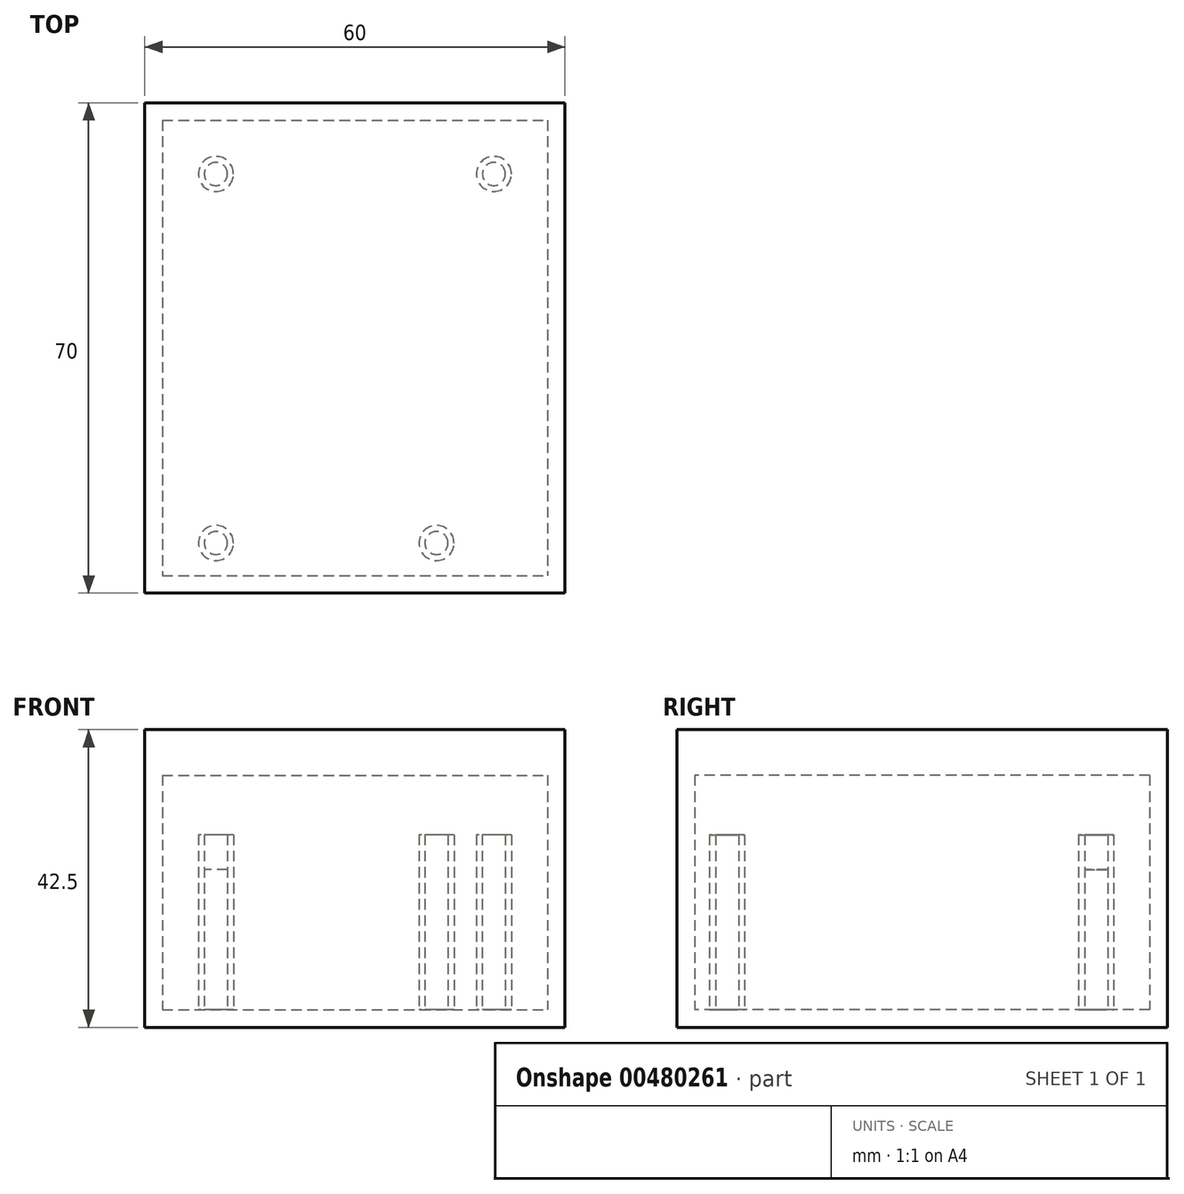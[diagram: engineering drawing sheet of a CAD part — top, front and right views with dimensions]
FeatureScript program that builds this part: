
annotation { "Feature Type Name" : "Feature", "Feature Type Description" : "" }
export const myFeature = defineFeature(function(context is Context, id is Id, definition is map)
    precondition{}
    {
        {
            var Q0;
            Q0=qCreatedBy(makeId("Top.planeOp"),FACE);
            var sketch = newSketch(context, id + "F0", { "sketchPlane" : qUnion([Q0])});
            skLineSegment(sketch, "E0.bottom", {"start": v(-30, 35) * mm, "end": v(30, 35) * mm});
            skLineSegment(sketch, "E0.top", {"start": v(-30, -35) * mm, "end": v(30, -35) * mm});
            skLineSegment(sketch, "E0.left", {"start": v(-30, 35) * mm, "end": v(-30, -35) * mm});
            skLineSegment(sketch, "E0.right", {"start": v(30, 35) * mm, "end": v(30, -35) * mm});
            skPoint(sketch, "E0.middle", {"position": v(0, 0) * mm});
            skSolve(sketch);
        }
        {
            var Q0;
            Q0=makeQuery(id+"F0.imprint","IMPRINT",FACE,{"disambiguationData":[TD([[makeQuery(id+"F0.imprint","IMPRINT",EDGE,{"derivedFrom":sQuery(id+"F0.wireOp",EDGE,"E0.bottom")}),-1.0]])]});
            extrude(context, id + "F1", {"entities" : qUnion([Q0]), "depth" : 40 * mm});
        }
        {
            var Q0;
            Q0=makeQuery(id+"F1.opExtrude","CAP_FACE",FACE,{"disambiguationData":[OSD([sQuery(id+"F0.wireOp",EDGE,"E0.bottom"),sQuery(id+"F0.wireOp",EDGE,"E0.top"),sQuery(id+"F0.wireOp",EDGE,"E0.left"),sQuery(id+"F0.wireOp",EDGE,"E0.right")])],"isStart":false});
            shell(context, id + "F2", {"entities" : qUnion([Q0]), "thickness" : 2.5 * mm});
        }
        {
            var Q0;
            Q0=makeQuery(id+"F1.opExtrude","CAP_FACE",FACE,{"disambiguationData":[OSD([sQuery(id+"F0.wireOp",EDGE,"E0.bottom"),sQuery(id+"F0.wireOp",EDGE,"E0.top"),sQuery(id+"F0.wireOp",EDGE,"E0.left"),sQuery(id+"F0.wireOp",EDGE,"E0.right")])],"isStart":false});
            var sketch = newSketch(context, id + "F3", { "sketchPlane" : qUnion([Q0])});
            skLineSegment(sketch, "E1.bottom", {"start": v(-27.5, 32.5) * mm, "end": v(27.5, 32.5) * mm});
            skLineSegment(sketch, "E1.top", {"start": v(-27.5, -32.5) * mm, "end": v(27.5, -32.5) * mm});
            skLineSegment(sketch, "E1.left", {"start": v(-27.5, 32.5) * mm, "end": v(-27.5, -32.5) * mm});
            skLineSegment(sketch, "E1.right", {"start": v(27.5, 32.5) * mm, "end": v(27.5, -32.5) * mm});
            skLineSegment(sketch, "E2.bottom", {"start": v(-30, 35) * mm, "end": v(30, 35) * mm});
            skLineSegment(sketch, "E2.top", {"start": v(-30, -35) * mm, "end": v(30, -35) * mm});
            skLineSegment(sketch, "E2.left", {"start": v(-30, 35) * mm, "end": v(-30, -35) * mm});
            skLineSegment(sketch, "E2.right", {"start": v(30, 35) * mm, "end": v(30, -35) * mm});
            skSolve(sketch);
        }
        {
            var Q0;
            Q0=makeQuery(id+"F3.imprint","IMPRINT",FACE,{"disambiguationData":[TD([[makeQuery(id+"F3.imprint","IMPRINT",EDGE,{"derivedFrom":sQuery(id+"F3.wireOp",EDGE,"E1.bottom")}),1.0]])]});
            var Q1;
            Q1=makeQuery(id+"F3.imprint","IMPRINT",FACE,{"disambiguationData":[TD([[makeQuery(id+"F3.imprint","IMPRINT",EDGE,{"derivedFrom":sQuery(id+"F3.wireOp",EDGE,"E1.bottom")}),-1.0]])]});
            extrude(context, id + "F4", {"entities" : qUnion([Q0, Q1]), "depth" : 2.5 * mm});
        }
        {
            var Q0;
            Q0=makeQuery(id+"F3.imprint","IMPRINT",FACE,{"disambiguationData":[TD([[makeQuery(id+"F3.imprint","IMPRINT",EDGE,{"derivedFrom":sQuery(id+"F3.wireOp",EDGE,"E1.bottom")}),-1.0]])]});
            extrude(context, id + "F5", {"entities" : qUnion([Q0]), "operationType" : NewBodyOperationType.ADD, "oppositeDirection" : true, "depth" : 4 * mm});
        }
        {
            var Q0;
            Q0=makeQuery(id+"F2.opShell","OFFSET_FACE",FACE,{"disambiguationData":[OSD([sQuery(id+"F0.wireOp",EDGE,"E0.bottom"),sQuery(id+"F0.wireOp",EDGE,"E0.top"),sQuery(id+"F0.wireOp",EDGE,"E0.left"),sQuery(id+"F0.wireOp",EDGE,"E0.right")])]});
            var sketch = newSketch(context, id + "F6", { "sketchPlane" : qUnion([Q0])});
            skCircle(sketch, "E3", {"center": v(-19.85, 24.85) * mm, "radius": 1.66 * mm});
            skCircle(sketch, "E4", {"center": v(-19.85, 24.85) * mm, "radius": 1.65 * mm});
            skCircle(sketch, "E5.MirrorC", {"center": v(19.85, 24.85) * mm, "radius": 1.65 * mm});
            skCircle(sketch, "E6", {"center": v(-19.85, -27.85) * mm, "radius": 1.65 * mm});
            skCircle(sketch, "E7", {"center": v(11.65, -27.85) * mm, "radius": 1.65 * mm});
            skCircle(sketch, "E8", {"center": v(-19.85, 24.85) * mm, "radius": 2.5 * mm});
            skCircle(sketch, "E9.MirrorC", {"center": v(19.85, 24.85) * mm, "radius": 2.5 * mm});
            skCircle(sketch, "E10", {"center": v(-19.85, -27.85) * mm, "radius": 2.5 * mm});
            skCircle(sketch, "E11", {"center": v(11.65, -27.85) * mm, "radius": 2.5 * mm});
            skSolve(sketch);
        }
        {
            var Q0;
            Q0 = qSketchRegion(id + "F6", true);
            extrude(context, id + "F7", {"entities" : qUnion([Q0]), "operationType" : NewBodyOperationType.ADD, "depth" : 25 * mm});
        }
        {
            var Q0;
            Q0 = qSketchRegion(id + "F6", true);
            var Q1;
            Q1=makeQuery(id+"F7.boolean.opBoolean","SPLIT",FACE,{"disambiguationData":[TD([makeQuery(id+"F7.opExtrude","SWEPT_FACE",FACE,{"disambiguationData":[OSD([sQuery(id+"F6.wireOp",EDGE,"E3")])]})])],"derivedFrom":makeQuery(id+"F2.opShell","OFFSET_FACE",FACE,{"disambiguationData":[OSD([sQuery(id+"F0.wireOp",EDGE,"E0.bottom"),sQuery(id+"F0.wireOp",EDGE,"E0.top"),sQuery(id+"F0.wireOp",EDGE,"E0.left"),sQuery(id+"F0.wireOp",EDGE,"E0.right")])]})});
            extrude(context, id + "F8", {"entities" : qUnion([Q0, Q1]), "operationType" : NewBodyOperationType.ADD, "depth" : 20 * mm});
        }
    });
